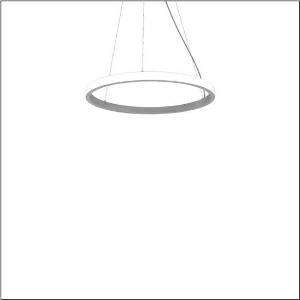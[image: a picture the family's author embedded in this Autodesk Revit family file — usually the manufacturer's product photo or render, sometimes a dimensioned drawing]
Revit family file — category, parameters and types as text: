
# Revit family: silica_21_ring-o_5pjbo2d3204a
name_source: partatom
category: Lighting Fixtures
units: mm (PartAtom-declared; Revit-internal decimal feet)

## family parameters
Cut with Voids When Loaded = No
Host = Face
Light Source = No
Part Type = Normal
Room Calculation Point = No
Round Connector Dimension = Use Diameter
Shared = No

## types (1)
- Silica 21 Ring-O (1 x LED, 4940 lm, 80 W, 4000K)
    Apparent Load = 80 VA
    CIE Flux Codes = 2 16 49 50 100
    Color Rendering = 80
    Color Temperature = 4000K
    Default Elevation = 1800 mm
    Description = Silica 21 Ring-O, suspended luminaire, of PMMA, frosted, light emission: outer ring side luminous distribution, primary light characteristic: symmetric, installation type: suspended mounting, LED, rated luminous flux: 4.940lm, luminous efficacy: 62lm/W, light colour: 840, colour temperature: 4000K, control gear: DALI 2, with terminal, 5-pole, mains connection: 230V, AC/DC, 0/50..60Hz, rated input power: 80W, housing, of extruded aluminium section, metallic grey (RAL 9006), diameter: 810mm, ceiling canopy, metallic grey (RAL 9006), protection rating (lamp compartment): IP40, insulation class (complete): insulation class I (protective earthing), certification: CE, impact resistance: IK02, permissible operating ambient temperature: 0..+35°C, packaging unit: 1 piece
    Height = 48 mm  [stored 0.15748 ft]
    Lamp = 1 x LED
    Lamp Light Flux = 4940 lm
    Lamp Power = 80 W
    Lamp count = 1
    Length = 810 mm
    Luminous efficacy = 62 lm/W
    Manufacturer = Siteco
    ModVariant = No
    Model = 5PJBO2D3204A
    Mounting Place = Ceiling
    Mounting Type = Pendant
    Number of Poles = 1
    OnlyDefault = Yes
    Power Factor = 1
    Product Name = Silica 21 Ring-O
    Product group = suspended luminaire
    ProductGroupID = 904
    Protection Class = Protection class I
    Protection Degree = IP 40
    RLX_Detail_Level = 1
    RLX_Emergency_Light_Flux = 0 lm
    RLX_Emergency_Type = 0
    RLX_Emergency_Type_DB = No
    RlxData = <blob elided: 13045 chars, md5=e062fa36>
    Socket = socket
    Standby Power = 0 W
    System Light Flux = 4940 lm
    System Power = 80 W
    Type Comments = Product without accessories
    Type Image = l_1251760.jpg
    URL = http://relux.com
    VarID = ---
    Voltage = 0 V
    Weight = 0.00 kg
    Width = 0 mm  [stored 0 ft]

note: [stored X ft] marks values corroborated as IEEE doubles in the binary element streams (Revit-internal decimal feet)

## geometry (parser evidence)
native form markers: Sweep x10
no freeform markers — native parametric forms only
